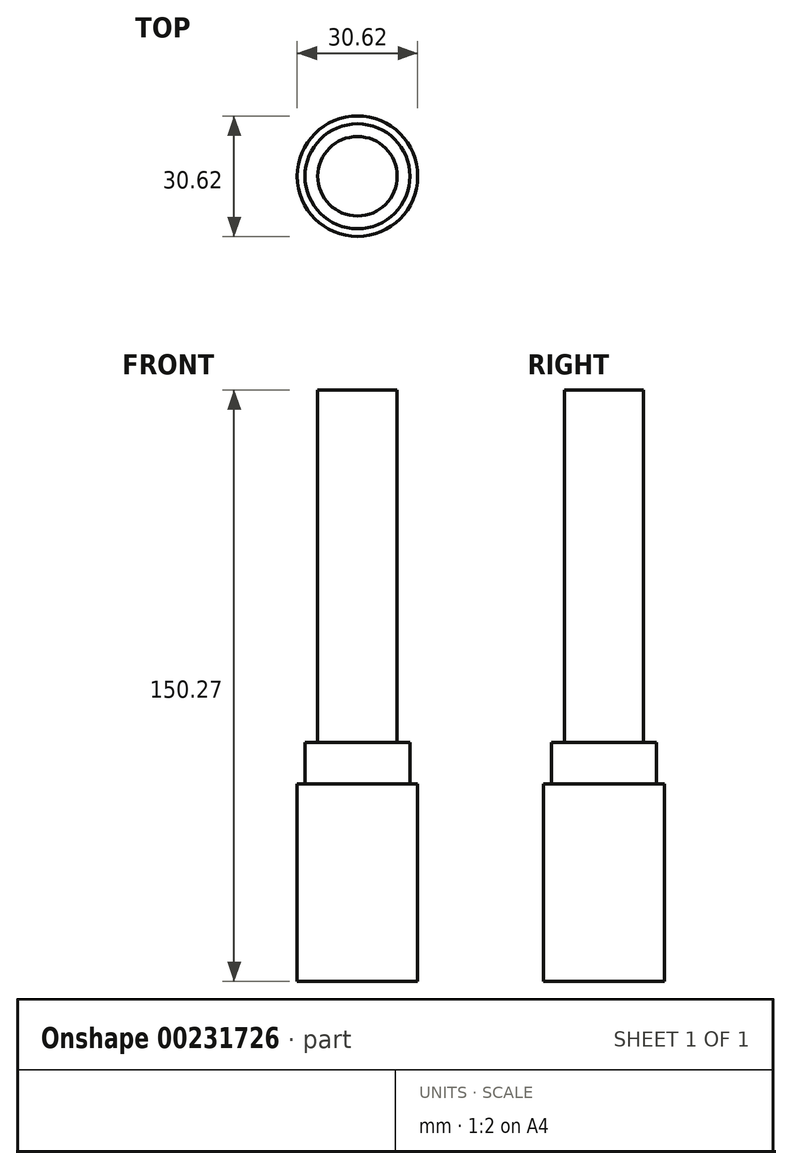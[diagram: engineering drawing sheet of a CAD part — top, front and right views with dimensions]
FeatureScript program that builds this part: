
annotation { "Feature Type Name" : "Feature", "Feature Type Description" : "" }
export const myFeature = defineFeature(function(context is Context, id is Id, definition is map)
    precondition{}
    {
        {
            var Q0;
            Q0=qCreatedBy(makeId("Top.planeOp"),FACE);
            var sketch = newSketch(context, id + "F0", { "sketchPlane" : qUnion([Q0])});
            skCircle(sketch, "E0", {"center": v(0, 0) * mm, "radius": 15.3 * mm});
            skSolve(sketch);
        }
        {
            var Q0;
            Q0 = qSketchRegion(id + "F0", true);
            extrude(context, id + "F1", {"entities" : qUnion([Q0]), "depth" : 150.27 * mm});
        }
        {
            var Q0;
            Q0=makeQuery(id+"F1.opExtrude","CAP_FACE",FACE,{"disambiguationData":[OSD([sQuery(id+"F0.wireOp",EDGE,"E0")])],"isStart":false});
            var sketch = newSketch(context, id + "F2", { "sketchPlane" : qUnion([Q0])});
            skCircle(sketch, "E1", {"center": v(0, 0) * mm, "radius": 13.33 * mm});
            skSolve(sketch);
        }
        {
            var Q0;
            Q0=makeQuery(id+"F2.imprint","IMPRINT",FACE,{"disambiguationData":[TD([[makeQuery(id+"F2.imprint","IMPRINT",EDGE,{"derivedFrom":sQuery(id+"F2.wireOp",EDGE,"E1")}),-1.0]])]});
            extrude(context, id + "F3", {"entities" : qUnion([Q0]), "operationType" : NewBodyOperationType.REMOVE, "oppositeDirection" : true, "depth" : 100.05 * mm});
        }
        {
            var Q0;
            Q0=makeQuery(id+"F1.opExtrude","CAP_FACE",FACE,{"disambiguationData":[OSD([sQuery(id+"F0.wireOp",EDGE,"E0")])],"isStart":false});
            var sketch = newSketch(context, id + "F4", { "sketchPlane" : qUnion([Q0])});
            skCircle(sketch, "E2", {"center": v(0, 0) * mm, "radius": 10.1 * mm});
            skSolve(sketch);
        }
        {
            var Q0;
            Q0=makeQuery(id+"F4.imprint","IMPRINT",FACE,{"disambiguationData":[TD([[makeQuery(id+"F4.imprint","IMPRINT",EDGE,{"derivedFrom":sQuery(id+"F4.wireOp",EDGE,"E2")}),-1.0]])]});
            extrude(context, id + "F5", {"entities" : qUnion([Q0]), "operationType" : NewBodyOperationType.REMOVE, "oppositeDirection" : true, "depth" : 89.58 * mm});
        }
    });
